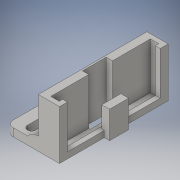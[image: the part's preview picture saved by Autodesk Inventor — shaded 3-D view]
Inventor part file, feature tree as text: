
AUTODESK INVENTOR PART (.ipt)
format: ipt  version: 2016 (Build 200138000, 138)  size: 293,376 bytes
history: native  units: in
note: dims shown in document units (in); Inventor stores cm internally (conversion verified against a paired STEP export)
features: sketch x15, extrude x14, fillet x1
ambient origin geometry x8: Origin, YZ Plane, XZ Plane, XY Plane, X Axis, Y Axis, Z Axis, Center Point
bodies: Solid1 (feature_tree)
feature tree (30):
  extrude  "Extrusion1"  Depth=0.08in
  extrude  "Extrusion5"  Depth=0.15in
  extrude  "Extrusion6"  Depth=0.16in
  extrude  "Extrusion7"  Depth=0.065in
  extrude  "Extrusion8"  Depth=0.15in
  extrude  "Extrusion9"  Depth=0.16in
  extrude  "Extrusion10"  Depth=0.45in
  extrude  "Extrusion11"  Depth=0.7175in
  extrude  "Extrusion12"  Depth=0.1in
  extrude  "Extrusion13"  Depth=0.7175in
  extrude  "Extrusion14"  Depth=1.755in
  extrude  "Extrusion15"  Depth=0.15in
  sketch  "Sketch24"  dims[d44=0.15in d45=0.815in d46=0.0in]
  sketch  "Sketch25"  dims[d54=0.25in d55=0.25in d56=0.25in]
  extrude  "Extrusion16"  Depth=0.815in TaperAngle=0.0deg
  extrude  "Extrusion17"  Depth=0.25in
  fillet  "Fillet1"  Radius=0.25in
  sketch  "Sketch1"  dims[d0=0.08in d1=0.08in]
  sketch  "Sketch10"  dims[d3=0.09in d5=0.15in]
  sketch  "Sketch11"  dims[d7=0.4in d8=0.16in]
  sketch  "Sketch12"  dims[d9=0.085in d10=0.065in]
  sketch  "Sketch14"  dims[d12=0.09in d13=0.15in]
  sketch  "Sketch16"  dims[d14=0.065in d15=0.16in]
  sketch  "Sketch17"  dims[d16=0.4in d17=0.45in]
  sketch  "Sketch18"  dims[d18=0.085in d19=0.7175in]
  sketch  "Sketch20"  dims[d21=0.245in d22=0.1in]
  sketch  "Sketch21"  dims[d23=0.1175in d24=0.0in d37=0.7175in]
  sketch  "Sketch22"  dims[d38=2.055in d39=1.755in]
  sketch  "Sketch23"  dims[d41=0.05in d42=0.0in d43=0.15in]
  sketch  "Sketch26"  dims[d57=0.4in d58=0.0in d59=0.4in d60=0.0in d63=0.6in d64=0.15in d65=0.0in d66=0.1562in d67=0.1562in d68=0.6in d69=0.3in d70=1.255in d72=0.3in d77=0.15in d78=0.0in d79=2.055in d80=0.8475in d82=0.4in d84=0.09in d85=0.0in d86=1.0in d87=0.0in d88=1.0in d89=0.0in d90=0.5625in d91=0.1in d92=1.0in d93=0.0in d94=1.0in d95=0.0in d96=1.0in d97=0.0in d98=0.16in d99=1.0in d100=0.0in d101=0.125in]
